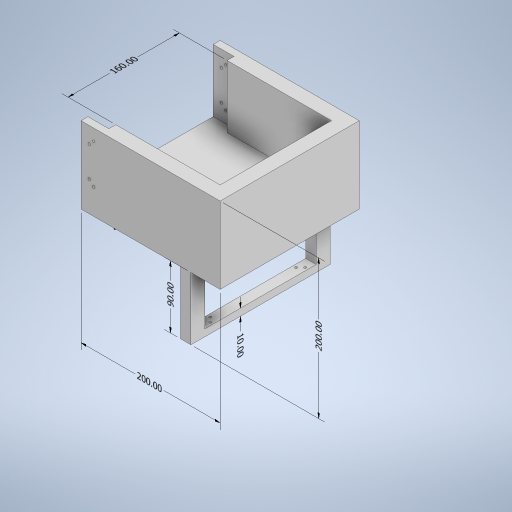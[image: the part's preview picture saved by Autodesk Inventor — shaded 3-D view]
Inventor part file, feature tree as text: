
AUTODESK INVENTOR PART (.ipt)
format: ipt  version: 2023 (Build 270158000, 158)  size: 362,496 bytes
history: native  units: mm
features: other x8, sketch x7, extrude x5, hole x2
ambient origin geometry x8: Origin, YZ Plane, XZ Plane, XY Plane, X Axis, Y Axis, Z Axis, Center Point
bodies: Body1 (feature_tree)
feature tree (22):
  other  "Sólido1"
  other  "Anotaciones"
  extrude  "Extrusión1"  Depth=200.0mm
  hole  "Agujero1"  [1 undecoded]
  extrude  "Extrusión2"  Depth=15.0mm
  extrude  "Extrusión3"  Depth=80.0mm TaperAngle=0.0deg
  extrude  "Extrusión4"  Depth=200.0mm
  extrude  "Extrusión5"  Depth=20.0mm
  hole  "Agujero2"  [1 undecoded]
  sketch  "Boceto2"  dims[d7=15.0mm d8=200.0mm]
  sketch  "Boceto3"  dims[d9=10.0mm d10=0.0mm]
  sketch  "Boceto4"  dims[d11=3.5mm d12=1.75mm d13=1.75mm d14=1.75mm d15=1.75mm d16=10.0mm d17=10.0mm d19=30.0mm]
  sketch  "Boceto5"  dims[d20=3.5mm d21=6.0mm d22=4.0mm d23=2.0mm d24=90.0deg d25=8.0mm d26=20.594885mm d27=15.0mm]
  sketch  "Boceto6"  dims[d28=20.0mm d29=80.0mm d30=0.0mm]
  sketch  "Boceto7"  dims[d31=57.0mm d32=200.0mm]
  sketch  "Boceto8"  dims[d33=110.0mm d34=0.0mm d36=20.0mm d37=20.0mm d38=20.0mm d39=90.0mm d40=0.0mm d43=30.0mm d44=0.0mm d45=3.5mm d46=1.75mm d47=1.75mm d48=1.75mm d49=1.75mm d50=10.0mm d51=10.0mm d52=15.0mm d53=10.0mm d54=10.0mm d55=15.0mm d56=3.5mm d57=6.0mm d58=4.0mm d59=2.0mm d60=90.0deg d61=8.0mm d62=20.594885mm d63=10.0mm d65=10.0mm d75=200.0mm d76=10.0mm d77=20.0mm d81=30.0mm d66=5.760865mm d67=7.72461mm d68=200.0mm d69=3.008686mm d70=2.422102mm d71=10.0mm d72=3.500509mm d73=2.402572mm d74=90.0mm d78=3.13122mm d79=6.269346mm d80=200.0mm d82=8.450127mm d83=0.968417mm d84=20.0mm d85=4.759975mm d86=4.646891mm d87=160.0mm]
  other  "Cota lineal 1"
  other  "Cota lineal 2"
  other  "Cota lineal 3"
  other  "Cota lineal 4"
  other  "Cota lineal 5"
  other  "Cota lineal 6"
note: 2 required parameter values undecoded (feature->parameter linkage not recoverable at this tier; creation-order binding heuristic only, values carry confidence <= 0.55)
